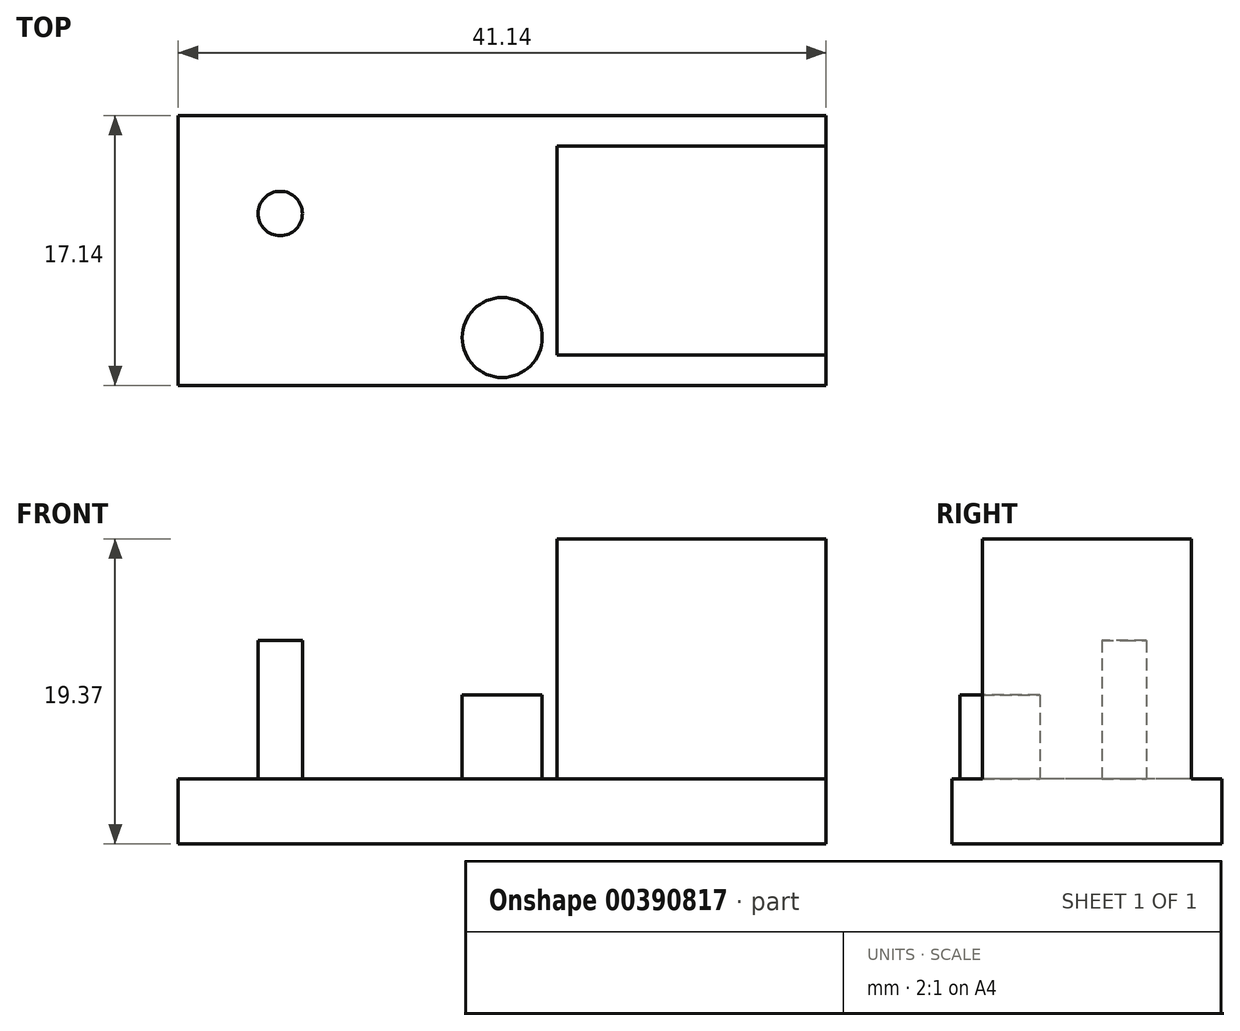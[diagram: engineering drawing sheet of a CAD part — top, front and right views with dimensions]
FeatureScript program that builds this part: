
annotation { "Feature Type Name" : "Feature", "Feature Type Description" : "" }
export const myFeature = defineFeature(function(context is Context, id is Id, definition is map)
    precondition{}
    {
        {
            var Q0;
            Q0=qCreatedBy(makeId("Top.planeOp"),FACE);
            var sketch = newSketch(context, id + "F0", { "sketchPlane" : qUnion([Q0])});
            skLineSegment(sketch, "E0.bottom", {"start": v(-20.57, 8.57) * mm, "end": v(20.57, 8.57) * mm});
            skLineSegment(sketch, "E0.top", {"start": v(-20.57, -8.57) * mm, "end": v(20.57, -8.57) * mm});
            skLineSegment(sketch, "E0.left", {"start": v(-20.57, 8.57) * mm, "end": v(-20.57, -8.57) * mm});
            skLineSegment(sketch, "E0.right", {"start": v(20.57, 8.57) * mm, "end": v(20.57, -8.57) * mm});
            skPoint(sketch, "E0.middle", {"position": v(0, 0) * mm});
            skLineSegment(sketch, "E1.bottom", {"start": v(20.57, 6.63) * mm, "end": v(3.48, 6.63) * mm});
            skLineSegment(sketch, "E1.top", {"start": v(20.57, -6.63) * mm, "end": v(3.48, -6.63) * mm});
            skLineSegment(sketch, "E1.left", {"start": v(20.57, 6.63) * mm, "end": v(20.57, -6.63) * mm});
            skLineSegment(sketch, "E1.right", {"start": v(3.48, 6.63) * mm, "end": v(3.48, -6.63) * mm});
            skLineSegment(sketch, "E2", {"start": v(-54.22, 0) * mm, "end": v(40.45, 0) * mm, "construction": true});
            skCircle(sketch, "E3", {"center": v(-14.1, 2.35) * mm, "radius": 1.4 * mm});
            skCircle(sketch, "E4", {"center": v(0, -5.52) * mm, "radius": 2.54 * mm});
            skSolve(sketch);
        }
        {
            var Q0;
            Q0 = qSketchRegion(id + "F0", true);
            var Q1;
            Q1=makeQuery(id+"F0.imprint","IMPRINT",FACE,{"disambiguationData":[TD([[makeQuery(id+"F0.imprint","IMPRINT",EDGE,{"derivedFrom":sQuery(id+"F0.wireOp",EDGE,"E4")}),1.0]])]});
            var Q2;
            Q2=makeQuery(id+"F0.imprint","IMPRINT",FACE,{"disambiguationData":[TD([[makeQuery(id+"F0.imprint","IMPRINT",EDGE,{"derivedFrom":sQuery(id+"F0.wireOp",EDGE,"E3")}),1.0]])]});
            extrude(context, id + "F1", {"entities" : qUnion([Q0, Q1, Q2]), "oppositeDirection" : true, "depth" : 4.13 * mm});
        }
        {
            var Q0;
            Q0=makeQuery(id+"F0.imprint","IMPRINT",FACE,{"disambiguationData":[TD([[makeQuery(id+"F0.imprint","IMPRINT",EDGE,{"derivedFrom":sQuery(id+"F0.wireOp",EDGE,"E1.bottom")}),1.0]])]});
            extrude(context, id + "F2", {"entities" : qUnion([Q0]), "operationType" : NewBodyOperationType.ADD, "depth" : 15.24 * mm});
        }
        {
            var Q0;
            Q0=makeQuery(id+"F0.imprint","IMPRINT",FACE,{"disambiguationData":[TD([[makeQuery(id+"F0.imprint","IMPRINT",EDGE,{"derivedFrom":sQuery(id+"F0.wireOp",EDGE,"E3")}),1.0]])]});
            extrude(context, id + "F3", {"entities" : qUnion([Q0]), "operationType" : NewBodyOperationType.ADD, "depth" : 8.79 * mm});
        }
        {
            var Q0;
            Q0=makeQuery(id+"F0.imprint","IMPRINT",FACE,{"disambiguationData":[TD([[makeQuery(id+"F0.imprint","IMPRINT",EDGE,{"derivedFrom":sQuery(id+"F0.wireOp",EDGE,"E4")}),1.0]])]});
            extrude(context, id + "F4", {"entities" : qUnion([Q0]), "operationType" : NewBodyOperationType.ADD, "depth" : 5.33 * mm});
        }
    });
